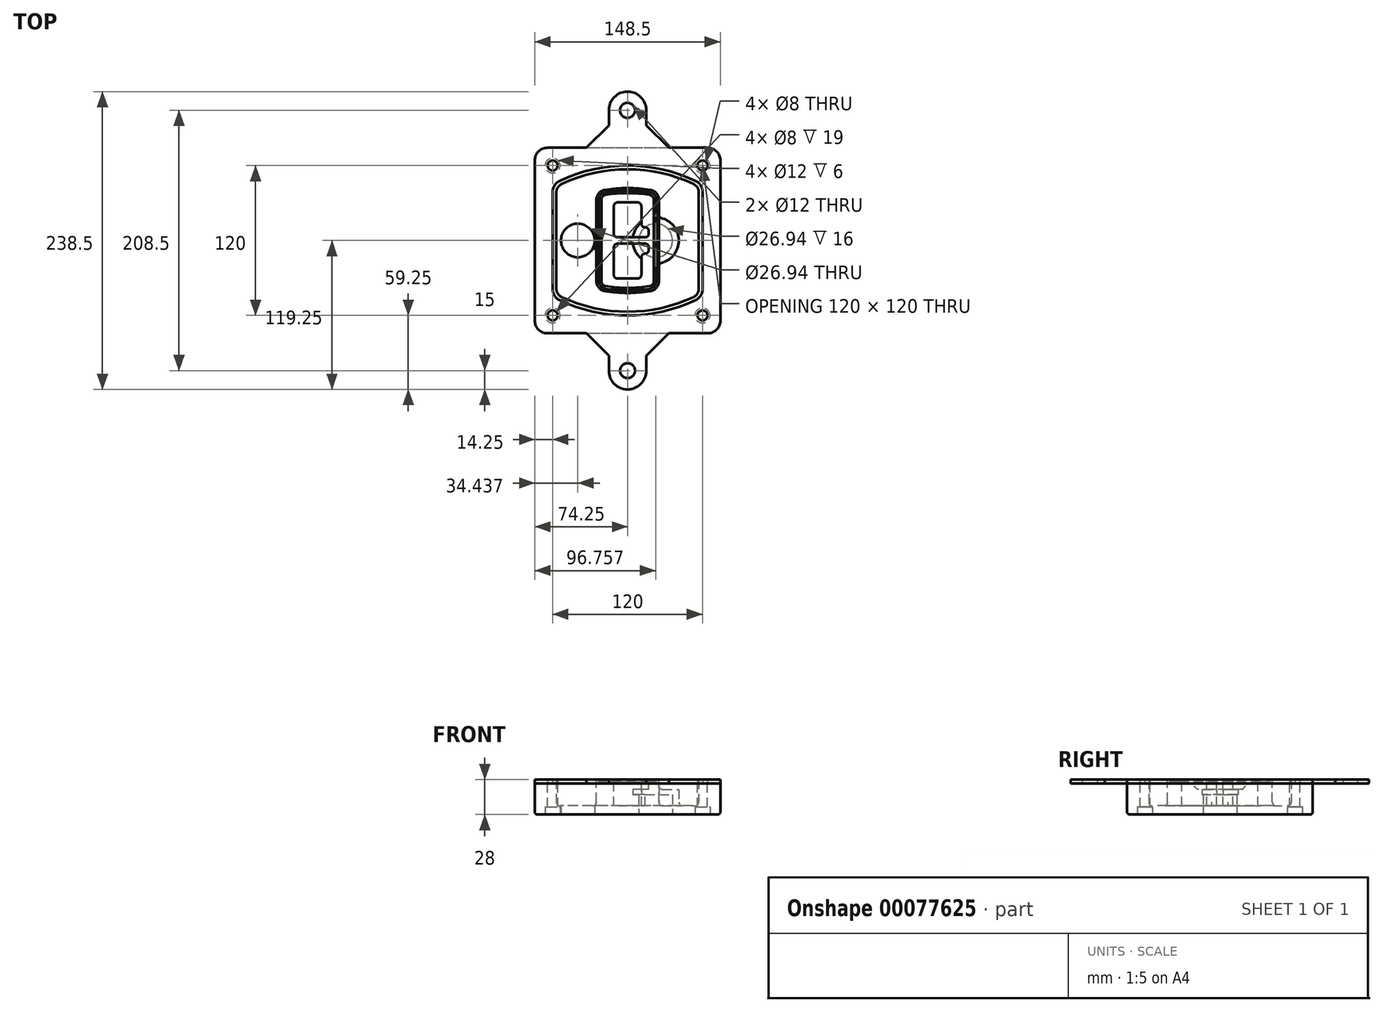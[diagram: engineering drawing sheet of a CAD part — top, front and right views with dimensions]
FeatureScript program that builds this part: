
annotation { "Feature Type Name" : "Feature", "Feature Type Description" : "" }
export const myFeature = defineFeature(function(context is Context, id is Id, definition is map)
    precondition{}
    {
        {
            var Q0;
            Q0=qCreatedBy(makeId("Top.planeOp"),FACE);
            var sketch = newSketch(context, id + "F0", { "sketchPlane" : qUnion([Q0])});
            skPoint(sketch, "E0.rect.middle", {"position": v(0, 0) * mm});
            skLineSegment(sketch, "E1.bottom", {"start": v(-64.25, -74.25) * mm, "end": v(64.25, -74.25) * mm});
            skLineSegment(sketch, "E1.top", {"start": v(-64.25, 74.25) * mm, "end": v(64.25, 74.25) * mm});
            skLineSegment(sketch, "E1.left", {"start": v(-74.25, -64.25) * mm, "end": v(-74.25, 64.25) * mm});
            skLineSegment(sketch, "E1.right", {"start": v(74.25, -64.25) * mm, "end": v(74.25, 64.25) * mm});
            skLineSegment(sketch, "E2", {"start": v(-74.25, 74.25) * mm, "end": v(74.25, -74.25) * mm, "construction": true});
            skLineSegment(sketch, "E3", {"start": v(74.25, 74.25) * mm, "end": v(-74.25, -74.25) * mm, "construction": true});
            skCircle(sketch, "E4", {"center": v(-60, 60) * mm, "radius": 4 * mm});
            skCircle(sketch, "E5", {"center": v(60, 60) * mm, "radius": 4 * mm});
            skCircle(sketch, "E6", {"center": v(60, -60) * mm, "radius": 4 * mm});
            skCircle(sketch, "E7", {"center": v(-60, -60) * mm, "radius": 4 * mm});
            skLineSegment(sketch, "E8", {"start": v(-60, 60) * mm, "end": v(60, 60) * mm, "construction": true});
            skLineSegment(sketch, "E9", {"start": v(60, 60) * mm, "end": v(60, -60) * mm, "construction": true});
            skLineSegment(sketch, "E10", {"start": v(60, -60) * mm, "end": v(-60, -60) * mm, "construction": true});
            skLineSegment(sketch, "E11", {"start": v(-60, -60) * mm, "end": v(-60, 60) * mm, "construction": true});
            skLineSegment(sketch, "E12", {"start": v(-60, 38.83) * mm, "end": v(-60, -38.83) * mm});
            skLineSegment(sketch, "E13", {"start": v(60, 38.83) * mm, "end": v(60, -38.83) * mm});
            skArc(sketch, "E14", {"start": v(54.26, 47.88) * mm, "mid": v(0, 60) * mm, "end": v(-54.26, 47.88) * mm});
            skArc(sketch, "E15", {"start": v(-54.26, -47.88) * mm, "mid": v(0, -60) * mm, "end": v(54.26, -47.88) * mm});
            skLineSegment(sketch, "E16", {"start": v(-60, 0) * mm, "end": v(60, 0) * mm, "construction": true});
            skPoint(sketch, "E17.visualSharp", {"position": v(-60, -45) * mm});
            skArc(sketch, "E17.filletArc", {"start": v(-60, -38.83) * mm, "mid": v(-58.44, -44.2) * mm, "end": v(-54.26, -47.88) * mm});
            skPoint(sketch, "E18.visualSharp", {"position": v(-60, 45) * mm});
            skArc(sketch, "E18.filletArc", {"start": v(-54.26, 47.88) * mm, "mid": v(-58.44, 44.2) * mm, "end": v(-60, 38.83) * mm});
            skPoint(sketch, "E19.visualSharp", {"position": v(60, 45) * mm});
            skArc(sketch, "E19.filletArc", {"start": v(60, 38.83) * mm, "mid": v(58.44, 44.2) * mm, "end": v(54.26, 47.88) * mm});
            skPoint(sketch, "E20.visualSharp", {"position": v(60, -45) * mm});
            skArc(sketch, "E20.filletArc", {"start": v(54.26, -47.88) * mm, "mid": v(58.44, -44.2) * mm, "end": v(60, -38.83) * mm});
            skPoint(sketch, "E21.visualSharp", {"position": v(-74.25, 74.25) * mm});
            skArc(sketch, "E21.filletArc", {"start": v(-64.25, 74.25) * mm, "mid": v(-71.32, 71.32) * mm, "end": v(-74.25, 64.25) * mm});
            skPoint(sketch, "E22.visualSharp", {"position": v(74.25, 74.25) * mm});
            skArc(sketch, "E22.filletArc", {"start": v(74.25, 64.25) * mm, "mid": v(71.32, 71.32) * mm, "end": v(64.25, 74.25) * mm});
            skPoint(sketch, "E23.visualSharp", {"position": v(74.25, -74.25) * mm});
            skArc(sketch, "E23.filletArc", {"start": v(64.25, -74.25) * mm, "mid": v(71.32, -71.32) * mm, "end": v(74.25, -64.25) * mm});
            skPoint(sketch, "E24.visualSharp", {"position": v(-74.25, -74.25) * mm});
            skArc(sketch, "E24.filletArc", {"start": v(-74.25, -64.25) * mm, "mid": v(-71.32, -71.32) * mm, "end": v(-64.25, -74.25) * mm});
            skArc(sketch, "E25.0", {"start": v(57, 38.83) * mm, "mid": v(55.9, 42.58) * mm, "end": v(52.98, 45.17) * mm});
            skLineSegment(sketch, "E25.1", {"start": v(57, 38.83) * mm, "end": v(57, -38.83) * mm});
            skArc(sketch, "E25.2", {"start": v(52.98, -45.17) * mm, "mid": v(55.9, -42.58) * mm, "end": v(57, -38.83) * mm});
            skArc(sketch, "E25.3", {"start": v(-52.98, -45.17) * mm, "mid": v(0, -57) * mm, "end": v(52.98, -45.17) * mm});
            skArc(sketch, "E25.4", {"start": v(-57, -38.83) * mm, "mid": v(-55.9, -42.58) * mm, "end": v(-52.98, -45.17) * mm});
            skArc(sketch, "E25.5", {"start": v(52.98, 45.17) * mm, "mid": v(0, 57) * mm, "end": v(-52.98, 45.17) * mm});
            skLineSegment(sketch, "E25.6", {"start": v(-57, 38.83) * mm, "end": v(-57, -38.83) * mm});
            skArc(sketch, "E25.7", {"start": v(-52.98, 45.17) * mm, "mid": v(-55.9, 42.58) * mm, "end": v(-57, 38.83) * mm});
            skArc(sketch, "E26.0", {"start": v(-55.96, 51.5) * mm, "mid": v(-61.82, 46.33) * mm, "end": v(-64, 38.83) * mm});
            skArc(sketch, "E26.1", {"start": v(55.96, 51.5) * mm, "mid": v(0, 64) * mm, "end": v(-55.96, 51.5) * mm});
            skArc(sketch, "E26.2", {"start": v(64, 38.83) * mm, "mid": v(61.82, 46.33) * mm, "end": v(55.96, 51.5) * mm});
            skLineSegment(sketch, "E26.3", {"start": v(64, 38.83) * mm, "end": v(64, -38.83) * mm});
            skArc(sketch, "E26.4", {"start": v(55.96, -51.5) * mm, "mid": v(61.82, -46.33) * mm, "end": v(64, -38.83) * mm});
            skLineSegment(sketch, "E26.5", {"start": v(-64, 38.83) * mm, "end": v(-64, -38.83) * mm});
            skArc(sketch, "E26.6", {"start": v(-55.96, -51.5) * mm, "mid": v(0, -64) * mm, "end": v(55.96, -51.5) * mm});
            skArc(sketch, "E26.7", {"start": v(-64, -38.83) * mm, "mid": v(-61.82, -46.33) * mm, "end": v(-55.96, -51.5) * mm});
            skSolve(sketch);
        }
        {
            var Q0;
            Q0=makeQuery(id+"F0.imprint","IMPRINT",FACE,{"disambiguationData":[TD([[makeQuery(id+"F0.imprint","IMPRINT",EDGE,{"derivedFrom":sQuery(id+"F0.wireOp",EDGE,"E1.bottom")}),1.0]])]});
            var Q1;
            Q1=makeQuery(id+"F0.imprint","IMPRINT",FACE,{"disambiguationData":[TD([[makeQuery(id+"F0.imprint","IMPRINT",EDGE,{"derivedFrom":sQuery(id+"F0.wireOp",EDGE,"E12")}),1.0]])]});
            var Q2;
            Q2=makeQuery(id+"F0.imprint","IMPRINT",FACE,{"disambiguationData":[TD([[makeQuery(id+"F0.imprint","IMPRINT",EDGE,{"derivedFrom":sQuery(id+"F0.wireOp",EDGE,"E25.0")}),1.0]])]});
            var Q3;
            Q3=makeQuery(id+"F0.imprint","IMPRINT",FACE,{"disambiguationData":[TD([[makeQuery(id+"F0.imprint","IMPRINT",EDGE,{"derivedFrom":sQuery(id+"F0.wireOp",EDGE,"E12")}),-1.0]])]});
            extrude(context, id + "F1", {"entities" : qUnion([Q0, Q1, Q2, Q3]), "oppositeDirection" : true, "depth" : 25 * mm});
        }
        {
            var Q0;
            Q0=makeQuery(id+"F0.imprint","IMPRINT",FACE,{"disambiguationData":[TD([[makeQuery(id+"F0.imprint","IMPRINT",EDGE,{"derivedFrom":sQuery(id+"F0.wireOp",EDGE,"E12")}),1.0]])]});
            extrude(context, id + "F2", {"entities" : qUnion([Q0]), "operationType" : NewBodyOperationType.ADD, "depth" : 3 * mm});
        }
        {
            var Q0;
            Q0=makeQuery(id+"F0.imprint","IMPRINT",FACE,{"disambiguationData":[TD([[makeQuery(id+"F0.imprint","IMPRINT",EDGE,{"derivedFrom":sQuery(id+"F0.wireOp",EDGE,"E25.0")}),1.0]])]});
            extrude(context, id + "F3", {"entities" : qUnion([Q0]), "operationType" : NewBodyOperationType.REMOVE, "oppositeDirection" : true, "depth" : 18 * mm});
        }
        {
            var Q0;
            Q0=makeQuery(id+"F2.opExtrude","CAP_FACE",FACE,{"disambiguationData":[OSD([sQuery(id+"F0.wireOp",EDGE,"E12"),sQuery(id+"F0.wireOp",EDGE,"E13"),sQuery(id+"F0.wireOp",EDGE,"E14"),sQuery(id+"F0.wireOp",EDGE,"E15"),sQuery(id+"F0.wireOp",EDGE,"E17.filletArc"),sQuery(id+"F0.wireOp",EDGE,"E18.filletArc"),sQuery(id+"F0.wireOp",EDGE,"E19.filletArc"),sQuery(id+"F0.wireOp",EDGE,"E20.filletArc"),sQuery(id+"F0.wireOp",EDGE,"E25.0"),sQuery(id+"F0.wireOp",EDGE,"E25.1"),sQuery(id+"F0.wireOp",EDGE,"E25.2"),sQuery(id+"F0.wireOp",EDGE,"E25.3"),sQuery(id+"F0.wireOp",EDGE,"E25.4"),sQuery(id+"F0.wireOp",EDGE,"E25.5"),sQuery(id+"F0.wireOp",EDGE,"E25.6"),sQuery(id+"F0.wireOp",EDGE,"E25.7")])],"isStart":false});
            var sketch = newSketch(context, id + "F4", { "sketchPlane" : qUnion([Q0])});
            skArc(sketch, "E27.0", {"start": v(-18.34, -40.45) * mm, "mid": v(0, -42) * mm, "end": v(18.34, -40.45) * mm});
            skArc(sketch, "E28.0", {"start": v(18.34, 40.45) * mm, "mid": v(0, 42) * mm, "end": v(-18.34, 40.45) * mm});
            skLineSegment(sketch, "E29", {"start": v(-25, 32.57) * mm, "end": v(-25, -32.57) * mm});
            skLineSegment(sketch, "E30", {"start": v(25, 32.57) * mm, "end": v(25, -32.57) * mm});
            skLineSegment(sketch, "E31", {"start": v(-25, 39.1) * mm, "end": v(25, 39.1) * mm, "construction": true});
            skLineSegment(sketch, "E32", {"start": v(-25, -39.1) * mm, "end": v(25, -39.1) * mm, "construction": true});
            skPoint(sketch, "E33.visualSharp", {"position": v(-25, 39.1) * mm});
            skArc(sketch, "E33.filletArc", {"start": v(-18.34, 40.45) * mm, "mid": v(-23.11, 37.73) * mm, "end": v(-25, 32.57) * mm});
            skPoint(sketch, "E34.visualSharp", {"position": v(25, 39.1) * mm});
            skArc(sketch, "E34.filletArc", {"start": v(25, 32.57) * mm, "mid": v(23.11, 37.73) * mm, "end": v(18.34, 40.45) * mm});
            skPoint(sketch, "E35.visualSharp", {"position": v(25, -39.1) * mm});
            skArc(sketch, "E35.filletArc", {"start": v(18.34, -40.45) * mm, "mid": v(23.11, -37.73) * mm, "end": v(25, -32.57) * mm});
            skPoint(sketch, "E36.visualSharp", {"position": v(-25, -39.1) * mm});
            skArc(sketch, "E36.filletArc", {"start": v(-25, -32.57) * mm, "mid": v(-23.11, -37.73) * mm, "end": v(-18.34, -40.45) * mm});
            skArc(sketch, "E37.0", {"start": v(52.98, 45.17) * mm, "mid": v(0, 57) * mm, "end": v(-52.98, 45.17) * mm});
            skArc(sketch, "E37.1", {"start": v(-52.98, 45.17) * mm, "mid": v(-55.9, 42.58) * mm, "end": v(-57, 38.83) * mm});
            skLineSegment(sketch, "E37.2", {"start": v(-57, 38.83) * mm, "end": v(-57, -38.83) * mm});
            skArc(sketch, "E37.3", {"start": v(-57, -38.83) * mm, "mid": v(-55.9, -42.58) * mm, "end": v(-52.98, -45.17) * mm});
            skArc(sketch, "E37.4", {"start": v(-52.98, -45.17) * mm, "mid": v(0, -57) * mm, "end": v(52.98, -45.17) * mm});
            skArc(sketch, "E37.5", {"start": v(52.98, -45.17) * mm, "mid": v(55.9, -42.58) * mm, "end": v(57, -38.83) * mm});
            skLineSegment(sketch, "E37.6", {"start": v(57, 38.83) * mm, "end": v(57, -38.83) * mm});
            skArc(sketch, "E37.7", {"start": v(57, 38.83) * mm, "mid": v(55.9, 42.58) * mm, "end": v(52.98, 45.17) * mm});
            skLineSegment(sketch, "E38.0", {"start": v(23, 32.57) * mm, "end": v(23, -32.57) * mm});
            skArc(sketch, "E38.1", {"start": v(18, -38.48) * mm, "mid": v(21.58, -36.44) * mm, "end": v(23, -32.57) * mm});
            skArc(sketch, "E38.2", {"start": v(-18, -38.48) * mm, "mid": v(0, -40) * mm, "end": v(18, -38.48) * mm});
            skArc(sketch, "E38.3", {"start": v(-23, -32.57) * mm, "mid": v(-21.58, -36.44) * mm, "end": v(-18, -38.48) * mm});
            skLineSegment(sketch, "E38.4", {"start": v(-23, 32.57) * mm, "end": v(-23, -32.57) * mm});
            skArc(sketch, "E38.5", {"start": v(23, 32.57) * mm, "mid": v(21.58, 36.44) * mm, "end": v(18, 38.48) * mm});
            skArc(sketch, "E38.6", {"start": v(-18, 38.48) * mm, "mid": v(-21.58, 36.44) * mm, "end": v(-23, 32.57) * mm});
            skArc(sketch, "E38.7", {"start": v(18, 38.48) * mm, "mid": v(0, 40) * mm, "end": v(-18, 38.48) * mm});
            skArc(sketch, "E39.0", {"start": v(21, 32.57) * mm, "mid": v(20.06, 35.15) * mm, "end": v(17.67, 36.5) * mm});
            skLineSegment(sketch, "E39.1", {"start": v(21, 32.57) * mm, "end": v(21, -32.57) * mm});
            skArc(sketch, "E39.2", {"start": v(17.67, -36.5) * mm, "mid": v(20.06, -35.15) * mm, "end": v(21, -32.57) * mm});
            skArc(sketch, "E39.3", {"start": v(-17.67, -36.5) * mm, "mid": v(0, -38) * mm, "end": v(17.67, -36.5) * mm});
            skArc(sketch, "E39.4", {"start": v(-21, -32.57) * mm, "mid": v(-20.06, -35.15) * mm, "end": v(-17.67, -36.5) * mm});
            skArc(sketch, "E39.5", {"start": v(17.67, 36.5) * mm, "mid": v(0, 38) * mm, "end": v(-17.67, 36.5) * mm});
            skLineSegment(sketch, "E39.6", {"start": v(-21, 32.57) * mm, "end": v(-21, -32.57) * mm});
            skArc(sketch, "E39.7", {"start": v(-17.67, 36.5) * mm, "mid": v(-20.06, 35.15) * mm, "end": v(-21, 32.57) * mm});
            skLineSegment(sketch, "E40", {"start": v(-25, 0) * mm, "end": v(25, 0) * mm, "construction": true});
            skLineSegment(sketch, "E41", {"start": v(-11, 5.5) * mm, "end": v(-11, 27.5) * mm});
            skLineSegment(sketch, "E42", {"start": v(-8, 30.5) * mm, "end": v(8, 30.5) * mm});
            skLineSegment(sketch, "E43", {"start": v(11, 27.5) * mm, "end": v(11, 13.5) * mm});
            skLineSegment(sketch, "E44", {"start": v(14, 10.5) * mm, "end": v(14, 10.5) * mm});
            skLineSegment(sketch, "E45", {"start": v(17, 7.5) * mm, "end": v(17, 5.5) * mm});
            skLineSegment(sketch, "E46", {"start": v(14, 2.5) * mm, "end": v(-8, 2.5) * mm});
            skPoint(sketch, "E47.visualSharp", {"position": v(-11, 30.5) * mm});
            skArc(sketch, "E47.filletArc", {"start": v(-8, 30.5) * mm, "mid": v(-10.12, 29.62) * mm, "end": v(-11, 27.5) * mm});
            skPoint(sketch, "E48.visualSharp", {"position": v(11, 30.5) * mm});
            skArc(sketch, "E48.filletArc", {"start": v(11, 27.5) * mm, "mid": v(10.12, 29.62) * mm, "end": v(8, 30.5) * mm});
            skPoint(sketch, "E49.visualSharp", {"position": v(11, 10.5) * mm});
            skArc(sketch, "E49.filletArc", {"start": v(11, 13.5) * mm, "mid": v(11.88, 11.38) * mm, "end": v(14, 10.5) * mm});
            skPoint(sketch, "E50.visualSharp", {"position": v(17, 10.5) * mm});
            skArc(sketch, "E50.filletArc", {"start": v(17, 7.5) * mm, "mid": v(16.12, 9.62) * mm, "end": v(14, 10.5) * mm});
            skPoint(sketch, "E51.visualSharp", {"position": v(17, 2.5) * mm});
            skArc(sketch, "E51.filletArc", {"start": v(14, 2.5) * mm, "mid": v(16.12, 3.38) * mm, "end": v(17, 5.5) * mm});
            skPoint(sketch, "E52.visualSharp", {"position": v(-11, 2.5) * mm});
            skArc(sketch, "E52.filletArc", {"start": v(-11, 5.5) * mm, "mid": v(-10.12, 3.38) * mm, "end": v(-8, 2.5) * mm});
            skLineSegment(sketch, "E53.0.MirrorCS", {"start": v(14, -2.5) * mm, "end": v(-8, -2.5) * mm});
            skArc(sketch, "E54.0.MirrorCS", {"start": v(-11, -5.5) * mm, "mid": v(-10.12, -3.38) * mm, "end": v(-8, -2.5) * mm});
            skLineSegment(sketch, "E55.0.MirrorCS", {"start": v(-11, -5.5) * mm, "end": v(-11, -27.5) * mm});
            skArc(sketch, "E56.0.MirrorCS", {"start": v(-8, -30.5) * mm, "mid": v(-10.12, -29.62) * mm, "end": v(-11, -27.5) * mm});
            skLineSegment(sketch, "E57.0.MirrorCS", {"start": v(-8, -30.5) * mm, "end": v(8, -30.5) * mm});
            skArc(sketch, "E58.0.MirrorCS", {"start": v(11, -27.5) * mm, "mid": v(10.12, -29.62) * mm, "end": v(8, -30.5) * mm});
            skLineSegment(sketch, "E59.0.MirrorCS", {"start": v(11, -27.5) * mm, "end": v(11, -13.5) * mm});
            skArc(sketch, "E60.0.MirrorCS", {"start": v(11, -13.5) * mm, "mid": v(11.88, -11.38) * mm, "end": v(14, -10.5) * mm});
            skArc(sketch, "E61.0.MirrorCS", {"start": v(17, -7.5) * mm, "mid": v(16.12, -9.62) * mm, "end": v(14, -10.5) * mm});
            skLineSegment(sketch, "E62.0.MirrorCS", {"start": v(17, -7.5) * mm, "end": v(17, -5.5) * mm});
            skArc(sketch, "E63.0.MirrorCS", {"start": v(14, -2.5) * mm, "mid": v(16.12, -3.38) * mm, "end": v(17, -5.5) * mm});
            skSolve(sketch);
        }
        {
            var Q0;
            Q0=makeQuery(id+"F4.imprint","IMPRINT",FACE,{"disambiguationData":[TD([[makeQuery(id+"F4.imprint","IMPRINT",EDGE,{"derivedFrom":sQuery(id+"F4.wireOp",EDGE,"E27.0")}),1.0]])]});
            var Q1;
            Q1=makeQuery(id+"F4.imprint","IMPRINT",FACE,{"disambiguationData":[TD([[makeQuery(id+"F4.imprint","IMPRINT",EDGE,{"derivedFrom":sQuery(id+"F4.wireOp",EDGE,"E38.0")}),-1.0]])]});
            var Q2;
            Q2=makeQuery(id+"F4.imprint","IMPRINT",FACE,{"disambiguationData":[TD([[makeQuery(id+"F4.imprint","IMPRINT",EDGE,{"derivedFrom":sQuery(id+"F4.wireOp",EDGE,"E39.0")}),1.0]])]});
            extrude(context, id + "F5", {"entities" : qUnion([Q0, Q1, Q2]), "operationType" : NewBodyOperationType.ADD, "endBound" : BoundingType.UP_TO_NEXT, "oppositeDirection" : true, "depth" : 25 * mm});
        }
        {
            var Q0;
            Q0=makeQuery(id+"F4.imprint","IMPRINT",FACE,{"disambiguationData":[TD([[makeQuery(id+"F4.imprint","IMPRINT",EDGE,{"derivedFrom":sQuery(id+"F4.wireOp",EDGE,"E38.0")}),-1.0]])]});
            extrude(context, id + "F6", {"entities" : qUnion([Q0]), "operationType" : NewBodyOperationType.REMOVE, "oppositeDirection" : true, "depth" : 2 * mm});
        }
        {
            var Q0;
            Q0=makeQuery(id+"F1.opExtrude","CAP_FACE",FACE,{"disambiguationData":[OSD([sQuery(id+"F0.wireOp",EDGE,"E1.bottom"),sQuery(id+"F0.wireOp",EDGE,"E1.top"),sQuery(id+"F0.wireOp",EDGE,"E1.left"),sQuery(id+"F0.wireOp",EDGE,"E1.right"),sQuery(id+"F0.wireOp",EDGE,"E4"),sQuery(id+"F0.wireOp",EDGE,"E5"),sQuery(id+"F0.wireOp",EDGE,"E6"),sQuery(id+"F0.wireOp",EDGE,"E7"),sQuery(id+"F0.wireOp",EDGE,"E21.filletArc"),sQuery(id+"F0.wireOp",EDGE,"E22.filletArc"),sQuery(id+"F0.wireOp",EDGE,"E23.filletArc"),sQuery(id+"F0.wireOp",EDGE,"E24.filletArc")])],"isStart":false});
            var sketch = newSketch(context, id + "F7", { "sketchPlane" : qUnion([Q0])});
            skCircle(sketch, "E64", {"center": v(22.5, 0) * mm, "radius": 13.47 * mm});
            skCircle(sketch, "E65", {"center": v(-39.81, 0) * mm, "radius": 13.47 * mm});
            skLineSegment(sketch, "E66", {"start": v(74.25, 0) * mm, "end": v(-74.25, 0) * mm});
            skCircle(sketch, "E67", {"center": v(22.5, 0) * mm, "radius": 18.47 * mm});
            skCircle(sketch, "E68", {"center": v(60, -60) * mm, "radius": 6 * mm});
            skCircle(sketch, "E69", {"center": v(-60, -60) * mm, "radius": 6 * mm});
            skCircle(sketch, "E70", {"center": v(-60, 60) * mm, "radius": 6 * mm});
            skCircle(sketch, "E71", {"center": v(60, 60) * mm, "radius": 6 * mm});
            skSolve(sketch);
        }
        {
            var Q0;
            {var subQ1=sQuery(id+"F7.wireOp",EDGE,"E66");var subQ4=sQuery(id+"F7.wireOp",EDGE,"E64");var subQ6=makeQuery(id+"F7.imprint","INTERSECT",VERTEX,{"disambiguationData":[OD(0.0)],"derivedFrom":[subQ4,subQ1]});Q0=makeQuery(id+"F7.imprint","IMPRINT",FACE,{"disambiguationData":[TD([[makeQuery(id+"F7.imprint","IMPRINT",EDGE,{"disambiguationData":[TD([[subQ6,-1.0]])],"derivedFrom":subQ4}),-1.0]])]});}
            var Q1;
            {var subQ0=sQuery(id+"F7.wireOp",EDGE,"E66");var subQ1=sQuery(id+"F7.wireOp",EDGE,"E64");var subQ3=makeQuery(id+"F7.imprint","INTERSECT",VERTEX,{"disambiguationData":[OD(0.0)],"derivedFrom":[subQ1,subQ0]});Q1=makeQuery(id+"F7.imprint","IMPRINT",FACE,{"disambiguationData":[TD([[makeQuery(id+"F7.imprint","IMPRINT",EDGE,{"disambiguationData":[TD([[subQ3,-1.0]])],"derivedFrom":subQ1}),1.0]])]});}
            var Q2;
            {var subQ0=sQuery(id+"F7.wireOp",EDGE,"E66");var subQ1=sQuery(id+"F7.wireOp",EDGE,"E64");var subQ3=makeQuery(id+"F7.imprint","INTERSECT",VERTEX,{"disambiguationData":[OD(0.0)],"derivedFrom":[subQ1,subQ0]});Q2=makeQuery(id+"F7.imprint","IMPRINT",FACE,{"disambiguationData":[TD([[makeQuery(id+"F7.imprint","IMPRINT",EDGE,{"disambiguationData":[TD([[subQ3,1.0]])],"derivedFrom":subQ1}),1.0]])]});}
            var Q3;
            {var subQ1=sQuery(id+"F7.wireOp",EDGE,"E66");var subQ4=sQuery(id+"F7.wireOp",EDGE,"E64");var subQ6=makeQuery(id+"F7.imprint","INTERSECT",VERTEX,{"disambiguationData":[OD(0.0)],"derivedFrom":[subQ4,subQ1]});Q3=makeQuery(id+"F7.imprint","IMPRINT",FACE,{"disambiguationData":[TD([[makeQuery(id+"F7.imprint","IMPRINT",EDGE,{"disambiguationData":[TD([[subQ6,1.0]])],"derivedFrom":subQ4}),-1.0]])]});}
            extrude(context, id + "F8", {"entities" : qUnion([Q0, Q1, Q2, Q3]), "operationType" : NewBodyOperationType.ADD, "oppositeDirection" : true, "depth" : 20 * mm});
        }
        {
            var Q0;
            {var subQ0=sQuery(id+"F7.wireOp",EDGE,"E66");var subQ1=sQuery(id+"F7.wireOp",EDGE,"E64");var subQ3=makeQuery(id+"F7.imprint","INTERSECT",VERTEX,{"disambiguationData":[OD(0.0)],"derivedFrom":[subQ1,subQ0]});Q0=makeQuery(id+"F7.imprint","IMPRINT",FACE,{"disambiguationData":[TD([[makeQuery(id+"F7.imprint","IMPRINT",EDGE,{"disambiguationData":[TD([[subQ3,-1.0]])],"derivedFrom":subQ1}),1.0]])]});}
            var Q1;
            {var subQ0=sQuery(id+"F7.wireOp",EDGE,"E66");var subQ1=sQuery(id+"F7.wireOp",EDGE,"E64");var subQ3=makeQuery(id+"F7.imprint","INTERSECT",VERTEX,{"disambiguationData":[OD(0.0)],"derivedFrom":[subQ1,subQ0]});Q1=makeQuery(id+"F7.imprint","IMPRINT",FACE,{"disambiguationData":[TD([[makeQuery(id+"F7.imprint","IMPRINT",EDGE,{"disambiguationData":[TD([[subQ3,1.0]])],"derivedFrom":subQ1}),1.0]])]});}
            extrude(context, id + "F9", {"entities" : qUnion([Q0, Q1]), "operationType" : NewBodyOperationType.REMOVE, "oppositeDirection" : true, "depth" : 16 * mm});
        }
        {
            var Q0;
            {var subQ0=sQuery(id+"F7.wireOp",EDGE,"E66");var subQ1=sQuery(id+"F7.wireOp",EDGE,"E65");var subQ3=makeQuery(id+"F7.imprint","INTERSECT",VERTEX,{"disambiguationData":[OD(0.0)],"derivedFrom":[subQ1,subQ0]});Q0=makeQuery(id+"F7.imprint","IMPRINT",FACE,{"disambiguationData":[TD([[makeQuery(id+"F7.imprint","IMPRINT",EDGE,{"disambiguationData":[TD([[subQ3,-1.0]])],"derivedFrom":subQ1}),1.0]])]});}
            var Q1;
            {var subQ0=sQuery(id+"F7.wireOp",EDGE,"E66");var subQ1=sQuery(id+"F7.wireOp",EDGE,"E65");var subQ3=makeQuery(id+"F7.imprint","INTERSECT",VERTEX,{"disambiguationData":[OD(0.0)],"derivedFrom":[subQ1,subQ0]});Q1=makeQuery(id+"F7.imprint","IMPRINT",FACE,{"disambiguationData":[TD([[makeQuery(id+"F7.imprint","IMPRINT",EDGE,{"disambiguationData":[TD([[subQ3,1.0]])],"derivedFrom":subQ1}),1.0]])]});}
            extrude(context, id + "F10", {"entities" : qUnion([Q0, Q1]), "operationType" : NewBodyOperationType.REMOVE, "oppositeDirection" : true, "depth" : 25 * mm});
        }
        {
            var Q0;
            Q0=makeQuery(id+"F7.imprint","IMPRINT",FACE,{"disambiguationData":[TD([[makeQuery(id+"F7.imprint","IMPRINT",EDGE,{"derivedFrom":sQuery(id+"F7.wireOp",EDGE,"E68")}),1.0]])]});
            var Q1;
            Q1=makeQuery(id+"F7.imprint","IMPRINT",FACE,{"disambiguationData":[TD([[makeQuery(id+"F7.imprint","IMPRINT",EDGE,{"derivedFrom":makeQuery(id+"F1.opExtrude","CAP_EDGE",EDGE,{"disambiguationData":[OSD([sQuery(id+"F0.wireOp",EDGE,"E5")])],"isStart":false})}),-1.0]])]});
            var Q2;
            Q2=makeQuery(id+"F7.imprint","IMPRINT",FACE,{"disambiguationData":[TD([[makeQuery(id+"F7.imprint","IMPRINT",EDGE,{"derivedFrom":sQuery(id+"F7.wireOp",EDGE,"E69")}),1.0]])]});
            var Q3;
            Q3=makeQuery(id+"F7.imprint","IMPRINT",FACE,{"disambiguationData":[TD([[makeQuery(id+"F7.imprint","IMPRINT",EDGE,{"derivedFrom":makeQuery(id+"F1.opExtrude","CAP_EDGE",EDGE,{"disambiguationData":[OSD([sQuery(id+"F0.wireOp",EDGE,"E4")])],"isStart":false})}),-1.0]])]});
            var Q4;
            Q4=makeQuery(id+"F7.imprint","IMPRINT",FACE,{"disambiguationData":[TD([[makeQuery(id+"F7.imprint","IMPRINT",EDGE,{"derivedFrom":sQuery(id+"F7.wireOp",EDGE,"E70")}),1.0]])]});
            var Q5;
            Q5=makeQuery(id+"F7.imprint","IMPRINT",FACE,{"disambiguationData":[TD([[makeQuery(id+"F7.imprint","IMPRINT",EDGE,{"derivedFrom":makeQuery(id+"F1.opExtrude","CAP_EDGE",EDGE,{"disambiguationData":[OSD([sQuery(id+"F0.wireOp",EDGE,"E7")])],"isStart":false})}),-1.0]])]});
            var Q6;
            Q6=makeQuery(id+"F7.imprint","IMPRINT",FACE,{"disambiguationData":[TD([[makeQuery(id+"F7.imprint","IMPRINT",EDGE,{"derivedFrom":sQuery(id+"F7.wireOp",EDGE,"E71")}),1.0]])]});
            var Q7;
            Q7=makeQuery(id+"F7.imprint","IMPRINT",FACE,{"disambiguationData":[TD([[makeQuery(id+"F7.imprint","IMPRINT",EDGE,{"derivedFrom":makeQuery(id+"F1.opExtrude","CAP_EDGE",EDGE,{"disambiguationData":[OSD([sQuery(id+"F0.wireOp",EDGE,"E6")])],"isStart":false})}),-1.0]])]});
            extrude(context, id + "F11", {"entities" : qUnion([Q0, Q1, Q2, Q3, Q4, Q5, Q6, Q7]), "operationType" : NewBodyOperationType.REMOVE, "oppositeDirection" : true, "depth" : 6 * mm});
        }
        {
            var Q0;
            Q0=makeQuery(id+"F9.boolean.opBoolean","COPY",FACE,{"derivedFrom":makeQuery(id+"F9.opExtrude","CAP_FACE",FACE,{"disambiguationData":[OSD([sQuery(id+"F7.wireOp",EDGE,"E64")])],"isStart":false})});
            var sketch = newSketch(context, id + "F12", { "sketchPlane" : qUnion([Q0])});
            skArc(sketch, "E72.0", {"start": v(11, 14.45) * mm, "mid": v(6.45, 9.13) * mm, "end": v(4.2, 2.5) * mm});
            skArc(sketch, "E72.1", {"start": v(4.2, -2.5) * mm, "mid": v(6.45, -9.13) * mm, "end": v(11, -14.45) * mm});
            skLineSegment(sketch, "E73", {"start": v(4.2, -2.5) * mm, "end": v(14, -2.5) * mm});
            skLineSegment(sketch, "E74.0", {"start": v(14, 2.5) * mm, "end": v(4.2, 2.5) * mm});
            skArc(sketch, "E74.1", {"start": v(14, 2.5) * mm, "mid": v(16.12, 3.38) * mm, "end": v(17, 5.5) * mm});
            skLineSegment(sketch, "E74.2", {"start": v(17, 7.5) * mm, "end": v(17, 5.5) * mm});
            skArc(sketch, "E74.3", {"start": v(17, 7.5) * mm, "mid": v(16.12, 9.62) * mm, "end": v(14, 10.5) * mm});
            skArc(sketch, "E74.4", {"start": v(11, 13.5) * mm, "mid": v(11.88, 11.38) * mm, "end": v(14, 10.5) * mm});
            skLineSegment(sketch, "E74.5", {"start": v(11, 14.45) * mm, "end": v(11, 13.5) * mm});
            skLineSegment(sketch, "E74.7", {"start": v(14, -2.5) * mm, "end": v(4.2, -2.5) * mm});
            skArc(sketch, "E74.8", {"start": v(14, -2.5) * mm, "mid": v(16.12, -3.38) * mm, "end": v(17, -5.5) * mm});
            skLineSegment(sketch, "E74.9", {"start": v(17, -7.5) * mm, "end": v(17, -5.5) * mm});
            skArc(sketch, "E74.10", {"start": v(17, -7.5) * mm, "mid": v(16.12, -9.62) * mm, "end": v(14, -10.5) * mm});
            skArc(sketch, "E74.11", {"start": v(11, -13.5) * mm, "mid": v(11.88, -11.38) * mm, "end": v(14, -10.5) * mm});
            skLineSegment(sketch, "E74.12", {"start": v(11, -14.45) * mm, "end": v(11, -13.5) * mm});
            skPoint(sketch, "E75.orphan", {"position": v(11, -27.5) * mm});
            skPoint(sketch, "E76.orphan", {"position": v(-8, -2.5) * mm});
            skPoint(sketch, "E77.orphan", {"position": v(-8, 2.5) * mm});
            skPoint(sketch, "E78.orphan", {"position": v(11, 27.5) * mm});
            skSolve(sketch);
        }
        {
            var Q0;
            {var subQ7=sQuery(id+"F12.wireOp",EDGE,"E72.0");var subQ14=sQuery(id+"F12.wireOp",EDGE,"E72.1");var subQ16=sQuery(id+"F12.wireOp",EDGE,"E74.1");var subQ18=sQuery(id+"F12.wireOp",EDGE,"E74.8");Q0=qUnion([makeQuery(id+"F12.imprint","IMPRINT",FACE,{"disambiguationData":[TD([[makeQuery(id+"F12.imprint","IMPRINT",EDGE,{"derivedFrom":subQ7}),1.0]])]}),makeQuery(id+"F12.imprint","IMPRINT",FACE,{"disambiguationData":[TD([[makeQuery(id+"F12.imprint","IMPRINT",EDGE,{"derivedFrom":subQ14}),1.0]])]}),makeQuery(id+"F12.imprint","IMPRINT",FACE,{"disambiguationData":[TD([[makeQuery(id+"F12.imprint","IMPRINT",EDGE,{"derivedFrom":subQ16}),1.0]])]}),makeQuery(id+"F12.imprint","IMPRINT",FACE,{"disambiguationData":[TD([[makeQuery(id+"F12.imprint","IMPRINT",EDGE,{"derivedFrom":subQ18}),-1.0]])]})]);}
            var Q1;
            Q1=makeQuery(id+"F5.boolean.opBoolean","SPLIT",FACE,{"disambiguationData":[TD([makeQuery(id+"F5.opExtrude","SWEPT_FACE",FACE,{"disambiguationData":[OSD([sQuery(id+"F4.wireOp",EDGE,"E41")])]})])],"derivedFrom":makeQuery(id+"F3.boolean.opBoolean","COPY",FACE,{"derivedFrom":makeQuery(id+"F3.opExtrude","CAP_FACE",FACE,{"disambiguationData":[OSD([sQuery(id+"F0.wireOp",EDGE,"E25.0"),sQuery(id+"F0.wireOp",EDGE,"E25.1"),sQuery(id+"F0.wireOp",EDGE,"E25.2"),sQuery(id+"F0.wireOp",EDGE,"E25.3"),sQuery(id+"F0.wireOp",EDGE,"E25.4"),sQuery(id+"F0.wireOp",EDGE,"E25.5"),sQuery(id+"F0.wireOp",EDGE,"E25.6"),sQuery(id+"F0.wireOp",EDGE,"E25.7")])],"isStart":false})})});
            extrude(context, id + "F13", {"entities" : qUnion([Q0]), "operationType" : NewBodyOperationType.REMOVE, "endBound" : BoundingType.UP_TO_SURFACE, "endBoundEntityFace" : qUnion([Q1]), "depth" : 25 * mm});
        }
        {
            var Q0;
            Q0=makeQuery(id+"F3.boolean.opBoolean","COPY",EDGE,{"derivedFrom":makeQuery(id+"F3.opExtrude","CAP_EDGE",EDGE,{"disambiguationData":[OSD([sQuery(id+"F0.wireOp",EDGE,"E25.6")])],"isStart":false})});
            var Q1;
            Q1=makeQuery(id+"F8.boolean.opBoolean","INTERSECT",EDGE,{"derivedFrom":[makeQuery(id+"F5.opExtrude","SWEPT_FACE",FACE,{"disambiguationData":[OSD([sQuery(id+"F4.wireOp",EDGE,"E30")])]}),makeQuery(id+"F8.opExtrude","CAP_FACE",FACE,{"disambiguationData":[OSD([sQuery(id+"F7.wireOp",EDGE,"E67")])],"isStart":false})]});
            var Q2;
            Q2=makeQuery(id+"F8.boolean.opBoolean","INTERSECT",EDGE,{"disambiguationData":[OD(1.0)],"derivedFrom":[makeQuery(id+"F5.opExtrude","SWEPT_FACE",FACE,{"disambiguationData":[OSD([sQuery(id+"F4.wireOp",EDGE,"E30")])]}),makeQuery(id+"F8.opExtrude","SWEPT_FACE",FACE,{"disambiguationData":[OSD([sQuery(id+"F7.wireOp",EDGE,"E67")])]})]});
            var Q3;
            {var subQ0=sQuery(id+"F4.wireOp",EDGE,"E30");Q3=makeQuery(id+"F8.boolean.opBoolean","SPLIT",EDGE,{"disambiguationData":[TD([makeQuery(id+"F5.opExtrude","SWEPT_FACE",FACE,{"disambiguationData":[OSD([sQuery(id+"F4.wireOp",EDGE,"E35.filletArc")])]})])],"derivedFrom":makeQuery(id+"F5.opExtrude","CAP_EDGE",EDGE,{"disambiguationData":[OSD([subQ0])],"isStart":false})});}
            var Q4;
            {var subQ0=sQuery(id+"F0.wireOp",EDGE,"E25.7");var subQ1=sQuery(id+"F0.wireOp",EDGE,"E25.1");var subQ2=sQuery(id+"F0.wireOp",EDGE,"E25.6");var subQ3=sQuery(id+"F0.wireOp",EDGE,"E25.5");var subQ4=sQuery(id+"F0.wireOp",EDGE,"E25.4");var subQ5=sQuery(id+"F0.wireOp",EDGE,"E25.0");var subQ6=sQuery(id+"F0.wireOp",EDGE,"E25.2");var subQ7=sQuery(id+"F0.wireOp",EDGE,"E25.3");Q4=makeQuery(id+"F8.boolean.opBoolean","INTERSECT",EDGE,{"derivedFrom":[makeQuery(id+"F5.boolean.opBoolean","SPLIT",FACE,{"disambiguationData":[TD([makeQuery(id+"F2.opExtrude","SWEPT_FACE",FACE,{"disambiguationData":[OSD([subQ5])]})])],"derivedFrom":makeQuery(id+"F3.boolean.opBoolean","COPY",FACE,{"derivedFrom":makeQuery(id+"F3.opExtrude","CAP_FACE",FACE,{"disambiguationData":[OSD([subQ5,subQ1,subQ6,subQ7,subQ4,subQ3,subQ2,subQ0])],"isStart":false})})}),makeQuery(id+"F8.opExtrude","SWEPT_FACE",FACE,{"disambiguationData":[OSD([sQuery(id+"F7.wireOp",EDGE,"E67")])]})]});}
            var Q5;
            Q5=makeQuery(id+"F8.boolean.opBoolean","INTERSECT",EDGE,{"disambiguationData":[OD(0.0)],"derivedFrom":[makeQuery(id+"F5.opExtrude","SWEPT_FACE",FACE,{"disambiguationData":[OSD([sQuery(id+"F4.wireOp",EDGE,"E30")])]}),makeQuery(id+"F8.opExtrude","SWEPT_FACE",FACE,{"disambiguationData":[OSD([sQuery(id+"F7.wireOp",EDGE,"E67")])]})]});
            fillet(context, id + "F14", {"entities" : qUnion([Q0, Q1, Q2, Q3, Q4, Q5]), "radius" : 3 * mm, "tangentPropagation" : true, "allowEdgeOverflow" : false});
        }
        {
            var Q0;
            Q0=makeQuery(id+"F1.opExtrude","CAP_EDGE",EDGE,{"disambiguationData":[OSD([sQuery(id+"F0.wireOp",EDGE,"E1.bottom")])],"isStart":false});
            fillet(context, id + "F15", {"entities" : qUnion([Q0]), "radius" : 2 * mm, "tangentPropagation" : true, "allowEdgeOverflow" : false});
        }
        {
            var Q0;
            {var subQ0=sQuery(id+"F0.wireOp",EDGE,"E22.filletArc");var subQ1=sQuery(id+"F0.wireOp",EDGE,"E7");var subQ2=sQuery(id+"F0.wireOp",EDGE,"E6");var subQ3=sQuery(id+"F0.wireOp",EDGE,"E5");var subQ4=sQuery(id+"F0.wireOp",EDGE,"E4");var subQ5=sQuery(id+"F0.wireOp",EDGE,"E1.bottom");var subQ6=sQuery(id+"F0.wireOp",EDGE,"E21.filletArc");var subQ7=sQuery(id+"F0.wireOp",EDGE,"E1.top");var subQ8=sQuery(id+"F0.wireOp",EDGE,"E1.left");var subQ9=sQuery(id+"F0.wireOp",EDGE,"E1.right");var subQ10=sQuery(id+"F0.wireOp",EDGE,"E23.filletArc");var subQ11=sQuery(id+"F0.wireOp",EDGE,"E24.filletArc");Q0=makeQuery(id+"F2.boolean.opBoolean","SPLIT",FACE,{"disambiguationData":[TD([makeQuery(id+"F1.opExtrude","SWEPT_FACE",FACE,{"disambiguationData":[OSD([subQ5])]})])],"derivedFrom":makeQuery(id+"F1.opExtrude","CAP_FACE",FACE,{"disambiguationData":[OSD([subQ5,subQ7,subQ8,subQ9,subQ4,subQ3,subQ2,subQ1,subQ6,subQ0,subQ10,subQ11])],"isStart":true})});}
            var sketch = newSketch(context, id + "F16", { "sketchPlane" : qUnion([Q0])});
            skLineSegment(sketch, "E79", {"start": v(-33, 74.25) * mm, "end": v(-15, 92.25) * mm});
            skLineSegment(sketch, "E80", {"start": v(-15, 92.25) * mm, "end": v(-15, 104.25) * mm});
            skLineSegment(sketch, "E81", {"start": v(33, 74.25) * mm, "end": v(15, 92.25) * mm});
            skLineSegment(sketch, "E82", {"start": v(15, 92.25) * mm, "end": v(15, 104.25) * mm});
            skArc(sketch, "E83", {"start": v(15, 104.25) * mm, "mid": v(0, 119.25) * mm, "end": v(-15, 104.25) * mm});
            skCircle(sketch, "E84", {"center": v(0, 104.25) * mm, "radius": 6 * mm});
            skLineSegment(sketch, "E85", {"start": v(0, 104.25) * mm, "end": v(0, 74.25) * mm, "construction": true});
            skLineSegment(sketch, "E86", {"start": v(-74.25, 0) * mm, "end": v(74.25, 0) * mm, "construction": true});
            skLineSegment(sketch, "E87.MirrorCS", {"start": v(33, -74.25) * mm, "end": v(15, -92.25) * mm});
            skLineSegment(sketch, "E88.MirrorCS", {"start": v(0, -104.25) * mm, "end": v(0, -74.25) * mm, "construction": true});
            skLineSegment(sketch, "E89.MirrorCS", {"start": v(15, -92.25) * mm, "end": v(15, -104.25) * mm});
            skCircle(sketch, "E90.MirrorC", {"center": v(0, -104.25) * mm, "radius": 6 * mm});
            skArc(sketch, "E91.MirrorCS", {"start": v(15, -104.25) * mm, "mid": v(0, -119.25) * mm, "end": v(-15, -104.25) * mm});
            skLineSegment(sketch, "E92.MirrorCS", {"start": v(-15, -92.25) * mm, "end": v(-15, -104.25) * mm});
            skLineSegment(sketch, "E93.MirrorCS", {"start": v(-33, -74.25) * mm, "end": v(-15, -92.25) * mm});
            skSolve(sketch);
        }
        {
            var Q0;
            {var subQ1=sQuery(id+"F16.wireOp",EDGE,"E79");Q0=makeQuery(id+"F16.imprint","IMPRINT",FACE,{"disambiguationData":[TD([[makeQuery(id+"F16.imprint","IMPRINT",EDGE,{"derivedFrom":subQ1}),-1.0]])]});}
            var Q1;
            Q1=makeQuery(id+"F16.imprint","IMPRINT",FACE,{"disambiguationData":[TD([[makeQuery(id+"F16.imprint","IMPRINT",EDGE,{"derivedFrom":makeQuery(id+"F1.opExtrude","CAP_EDGE",EDGE,{"disambiguationData":[OSD([sQuery(id+"F0.wireOp",EDGE,"E1.left")])],"isStart":true})}),-1.0]])]});
            var Q2;
            {var subQ0=sQuery(id+"F16.wireOp",EDGE,"E87.MirrorCS");Q2=makeQuery(id+"F16.imprint","IMPRINT",FACE,{"disambiguationData":[TD([[makeQuery(id+"F16.imprint","IMPRINT",EDGE,{"derivedFrom":subQ0}),-1.0]])]});}
            var Q3;
            Q3=makeQuery(id+"F2.opExtrude","CAP_FACE",FACE,{"disambiguationData":[OSD([sQuery(id+"F0.wireOp",EDGE,"E12"),sQuery(id+"F0.wireOp",EDGE,"E13"),sQuery(id+"F0.wireOp",EDGE,"E14"),sQuery(id+"F0.wireOp",EDGE,"E15"),sQuery(id+"F0.wireOp",EDGE,"E17.filletArc"),sQuery(id+"F0.wireOp",EDGE,"E18.filletArc"),sQuery(id+"F0.wireOp",EDGE,"E19.filletArc"),sQuery(id+"F0.wireOp",EDGE,"E20.filletArc"),sQuery(id+"F0.wireOp",EDGE,"E25.0"),sQuery(id+"F0.wireOp",EDGE,"E25.1"),sQuery(id+"F0.wireOp",EDGE,"E25.2"),sQuery(id+"F0.wireOp",EDGE,"E25.3"),sQuery(id+"F0.wireOp",EDGE,"E25.4"),sQuery(id+"F0.wireOp",EDGE,"E25.5"),sQuery(id+"F0.wireOp",EDGE,"E25.6"),sQuery(id+"F0.wireOp",EDGE,"E25.7")])],"isStart":false});
            extrude(context, id + "F17", {"entities" : qUnion([Q0, Q1, Q2]), "endBound" : BoundingType.UP_TO_SURFACE, "endBoundEntityFace" : qUnion([Q3]), "depth" : 25 * mm});
        }
    });
